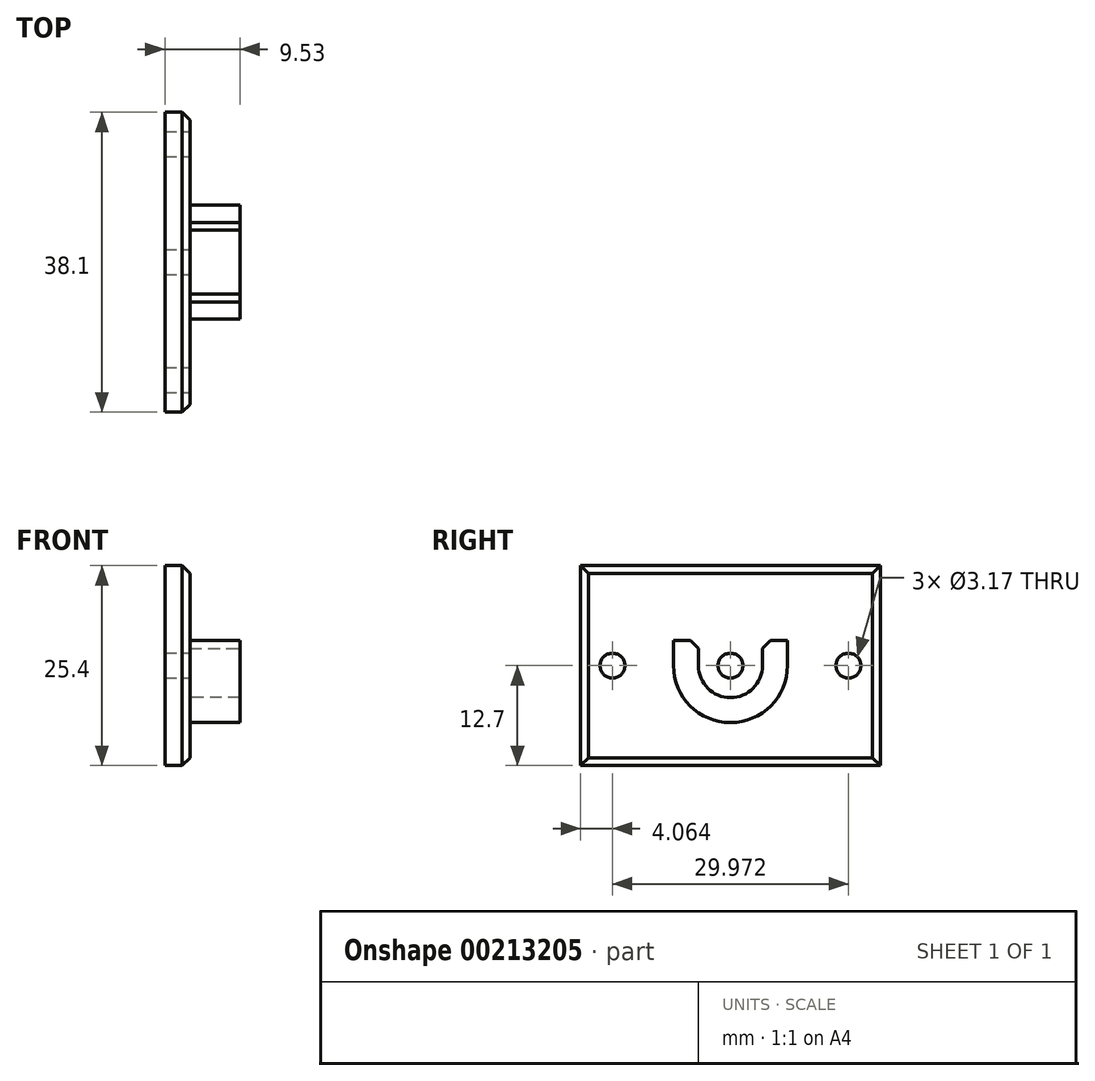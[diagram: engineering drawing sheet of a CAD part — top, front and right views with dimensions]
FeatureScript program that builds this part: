
annotation { "Feature Type Name" : "Feature", "Feature Type Description" : "" }
export const myFeature = defineFeature(function(context is Context, id is Id, definition is map)
    precondition{}
    {
        {
            var Q0;
            Q0=qCreatedBy(makeId("Right.planeOp"),FACE);
            var sketch = newSketch(context, id + "F0", { "sketchPlane" : qUnion([Q0])});
            skLineSegment(sketch, "E0.bottom", {"start": v(-19.05, 12.7) * mm, "end": v(19.05, 12.7) * mm});
            skLineSegment(sketch, "E0.top", {"start": v(-19.05, -12.7) * mm, "end": v(19.05, -12.7) * mm});
            skLineSegment(sketch, "E0.left", {"start": v(-19.05, 12.7) * mm, "end": v(-19.05, -12.7) * mm});
            skLineSegment(sketch, "E0.right", {"start": v(19.05, 12.7) * mm, "end": v(19.05, -12.7) * mm});
            skPoint(sketch, "E0.middle", {"position": v(0, 0) * mm});
            skSolve(sketch);
        }
        {
            var Q0;
            Q0 = qSketchRegion(id + "F0", true);
            extrude(context, id + "F1", {"entities" : qUnion([Q0]), "depth" : 3.17 * mm});
        }
        {
            var Q0;
            Q0=makeQuery(id+"F1.opExtrude","CAP_FACE",FACE,{"disambiguationData":[OSD([sQuery(id+"F0.wireOp",EDGE,"E0.bottom"),sQuery(id+"F0.wireOp",EDGE,"E0.top"),sQuery(id+"F0.wireOp",EDGE,"E0.left"),sQuery(id+"F0.wireOp",EDGE,"E0.right")])],"isStart":false});
            var sketch = newSketch(context, id + "F2", { "sketchPlane" : qUnion([Q0])});
            skArc(sketch, "E1", {"start": v(-4.06, 0) * mm, "mid": v(0, -4.06) * mm, "end": v(4.06, 0) * mm});
            skArc(sketch, "E2.0", {"start": v(-7.24, 0) * mm, "mid": v(0, -7.24) * mm, "end": v(7.24, 0) * mm});
            skLineSegment(sketch, "E3.0", {"start": v(-4.06, 3.18) * mm, "end": v(-7.24, 3.18) * mm});
            skLineSegment(sketch, "E4.0", {"start": v(4.06, 3.18) * mm, "end": v(7.24, 3.18) * mm});
            skLineSegment(sketch, "E5", {"start": v(-4.06, 3.18) * mm, "end": v(-4.06, 0) * mm});
            skLineSegment(sketch, "E6", {"start": v(-7.24, 3.18) * mm, "end": v(-7.24, 0) * mm});
            skLineSegment(sketch, "E7", {"start": v(4.06, 0) * mm, "end": v(4.06, 3.18) * mm});
            skLineSegment(sketch, "E8", {"start": v(7.24, 0) * mm, "end": v(7.24, 3.18) * mm});
            skSolve(sketch);
        }
        {
            var Q0;
            Q0 = qSketchRegion(id + "F2", true);
            extrude(context, id + "F3", {"entities" : qUnion([Q0]), "operationType" : NewBodyOperationType.ADD, "depth" : 6.35 * mm});
        }
        {
            var Q0;
            Q0=makeQuery(id+"F1.opExtrude","CAP_FACE",FACE,{"disambiguationData":[OSD([sQuery(id+"F0.wireOp",EDGE,"E0.bottom"),sQuery(id+"F0.wireOp",EDGE,"E0.top"),sQuery(id+"F0.wireOp",EDGE,"E0.left"),sQuery(id+"F0.wireOp",EDGE,"E0.right")])],"isStart":false});
            var sketch = newSketch(context, id + "F4", { "sketchPlane" : qUnion([Q0])});
            skCircle(sketch, "E9", {"center": v(-14.99, 0) * mm, "radius": 1.59 * mm});
            skCircle(sketch, "E10", {"center": v(14.99, 0) * mm, "radius": 1.59 * mm});
            skCircle(sketch, "E11", {"center": v(0, 0) * mm, "radius": 1.59 * mm});
            skSolve(sketch);
        }
        {
            var Q0;
            Q0 = qSketchRegion(id + "F4", true);
            extrude(context, id + "F5", {"entities" : qUnion([Q0]), "operationType" : NewBodyOperationType.REMOVE, "endBound" : BoundingType.UP_TO_NEXT, "oppositeDirection" : true, "depth" : 25.4 * mm});
        }
        {
            var Q0;
            Q0=makeQuery(id+"F3.opExtrude","SWEPT_EDGE",EDGE,{"disambiguationData":[OSD([sQuery(id+"F2.wireOp",EDGE,"E3.0"),sQuery(id+"F2.wireOp",EDGE,"E5")])]});
            var Q1;
            Q1=makeQuery(id+"F3.opExtrude","SWEPT_EDGE",EDGE,{"disambiguationData":[OSD([sQuery(id+"F2.wireOp",EDGE,"E4.0"),sQuery(id+"F2.wireOp",EDGE,"E7")])]});
            var Q2;
            Q2=makeQuery(id+"F1.opExtrude","CAP_EDGE",EDGE,{"disambiguationData":[OSD([sQuery(id+"F0.wireOp",EDGE,"E0.left")])],"isStart":false});
            var Q3;
            Q3=makeQuery(id+"F1.opExtrude","CAP_EDGE",EDGE,{"disambiguationData":[OSD([sQuery(id+"F0.wireOp",EDGE,"E0.bottom")])],"isStart":false});
            var Q4;
            Q4=makeQuery(id+"F1.opExtrude","CAP_EDGE",EDGE,{"disambiguationData":[OSD([sQuery(id+"F0.wireOp",EDGE,"E0.right")])],"isStart":false});
            var Q5;
            Q5=makeQuery(id+"F1.opExtrude","CAP_EDGE",EDGE,{"disambiguationData":[OSD([sQuery(id+"F0.wireOp",EDGE,"E0.top")])],"isStart":false});
            var Q6;
            Q6=makeQuery(id+"F3.opExtrude","CAP_EDGE",EDGE,{"disambiguationData":[OSD([sQuery(id+"F2.wireOp",EDGE,"E2.0")])],"isStart":true});
            var Q7;
            Q7=makeQuery(id+"F3.opExtrude","CAP_EDGE",EDGE,{"disambiguationData":[OSD([sQuery(id+"F2.wireOp",EDGE,"E6")])],"isStart":true});
            var Q8;
            Q8=makeQuery(id+"F3.opExtrude","CAP_EDGE",EDGE,{"disambiguationData":[OSD([sQuery(id+"F2.wireOp",EDGE,"E8")])],"isStart":true});
            chamfer(context, id + "F6", {"entities" : qUnion([Q0, Q1, Q2, Q3, Q4, Q5, Q6, Q7, Q8]), "width" : 1 * mm});
        }
    });
